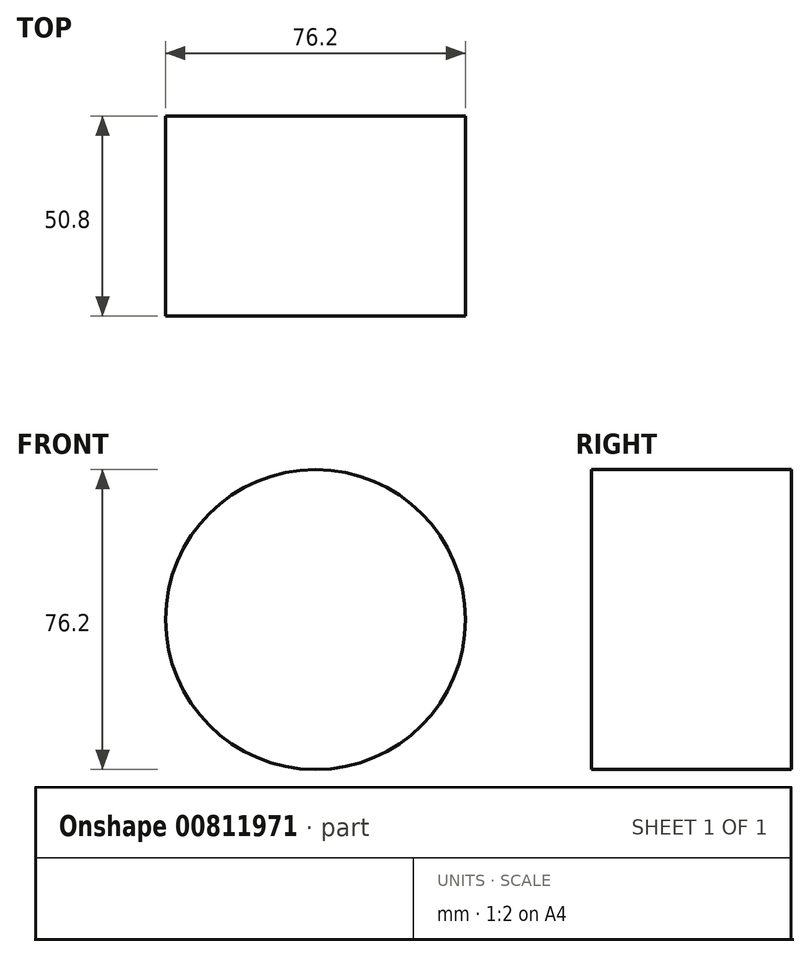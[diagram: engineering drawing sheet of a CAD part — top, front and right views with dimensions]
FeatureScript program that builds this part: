
annotation { "Feature Type Name" : "Feature", "Feature Type Description" : "" }
export const myFeature = defineFeature(function(context is Context, id is Id, definition is map)
    precondition{}
    {
        {
            var Q0;
            Q0=qCreatedBy(makeId("Front.planeOp"),FACE);
            var sketch = newSketch(context, id + "F0", { "sketchPlane" : qUnion([Q0])});
            skCircle(sketch, "E0", {"center": v(0, 0) * mm, "radius": 38.1 * mm});
            skSolve(sketch);
        }
        {
            var Q0;
            Q0=makeQuery(id+"F0.imprint","IMPRINT",FACE,{"disambiguationData":[TD([[makeQuery(id+"F0.imprint","IMPRINT",EDGE,{"derivedFrom":sQuery(id+"F0.wireOp",EDGE,"E0")}),1.0]])]});
            extrude(context, id + "F1", {"entities" : qUnion([Q0]), "depth" : 50.8 * mm, "offsetDistance" : 25.4 * mm});
        }
    });
